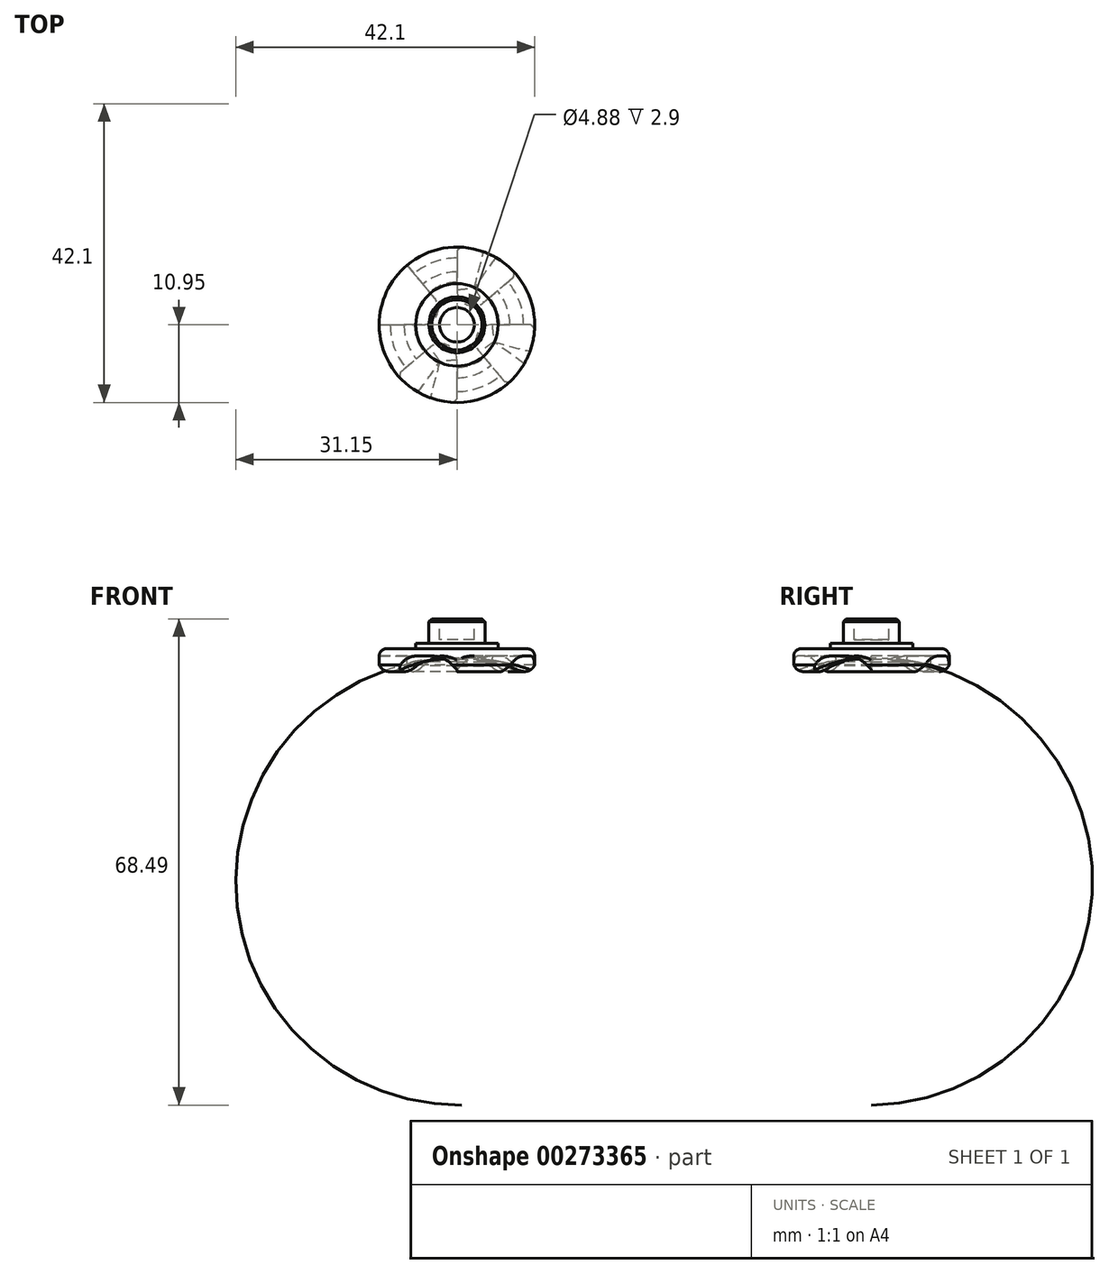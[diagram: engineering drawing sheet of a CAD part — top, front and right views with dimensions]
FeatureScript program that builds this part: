
annotation { "Feature Type Name" : "Feature", "Feature Type Description" : "" }
export const myFeature = defineFeature(function(context is Context, id is Id, definition is map)
    precondition{}
    {
        {
            var Q0;
            Q0=qCreatedBy(makeId("Top.planeOp"),FACE);
            var sketch = newSketch(context, id + "F0", { "sketchPlane" : qUnion([Q0])});
            skCircle(sketch, "E0", {"center": v(0, 0) * mm, "radius": 10.95 * mm});
            skSolve(sketch);
        }
        {
            var Q0;
            Q0=makeQuery(id+"F0.imprint","IMPRINT",FACE,{"disambiguationData":[TD([[makeQuery(id+"F0.imprint","IMPRINT",EDGE,{"derivedFrom":sQuery(id+"F0.wireOp",EDGE,"E0")}),1.0]])]});
            extrude(context, id + "F1", {"entities" : qUnion([Q0]), "depth" : 1 * mm, "offsetDistance" : 25 * mm});
        }
        {
            var Q0;
            Q0=makeQuery(id+"F1.opExtrude","CAP_FACE",FACE,{"disambiguationData":[OSD([sQuery(id+"F0.wireOp",EDGE,"E0")])],"isStart":true});
            var sketch = newSketch(context, id + "F2", { "sketchPlane" : qUnion([Q0])});
            skLineSegment(sketch, "E1", {"start": v(-10.95, 0) * mm, "end": v(-4.95, 0) * mm});
            skLineSegment(sketch, "E2", {"start": v(-7.04, -8.39) * mm, "end": v(-3.18, -3.8) * mm});
            skArc(sketch, "E3", {"start": v(-3.18, -3.8) * mm, "mid": v(-2.86, -1.33) * mm, "end": v(-4.95, 0) * mm});
            skArc(sketch, "E4.1.0", {"start": v(3.8, -3.18) * mm, "mid": v(1.33, -2.86) * mm, "end": v(0, -4.95) * mm});
            skLineSegment(sketch, "E4.1.1", {"start": v(8.39, -7.04) * mm, "end": v(3.8, -3.18) * mm});
            skLineSegment(sketch, "E4.1.2", {"start": v(0, -10.95) * mm, "end": v(0, -4.95) * mm});
            skArc(sketch, "E4.2.0", {"start": v(3.18, 3.8) * mm, "mid": v(2.86, 1.33) * mm, "end": v(4.95, 0) * mm});
            skLineSegment(sketch, "E4.2.1", {"start": v(7.04, 8.39) * mm, "end": v(3.18, 3.8) * mm});
            skLineSegment(sketch, "E4.2.2", {"start": v(10.95, 0) * mm, "end": v(4.95, 0) * mm});
            skArc(sketch, "E4.3.0", {"start": v(-3.8, 3.18) * mm, "mid": v(-1.33, 2.86) * mm, "end": v(0, 4.95) * mm});
            skLineSegment(sketch, "E4.3.1", {"start": v(-8.39, 7.04) * mm, "end": v(-3.8, 3.18) * mm});
            skLineSegment(sketch, "E4.3.2", {"start": v(0, 10.95) * mm, "end": v(0, 4.95) * mm});
            skPoint(sketch, "E4.center", {"position": v(0, 0) * mm});
            skSolve(sketch);
        }
        {
            var Q0;
            {var subQ4=sQuery(id+"F2.wireOp",EDGE,"E1");Q0=makeQuery(id+"F2.imprint","IMPRINT",FACE,{"disambiguationData":[TD([[makeQuery(id+"F2.imprint","IMPRINT",EDGE,{"derivedFrom":subQ4}),1.0]])]});}
            extrude(context, id + "F3", {"entities" : qUnion([Q0]), "operationType" : NewBodyOperationType.ADD, "depth" : 2.8 * mm, "offsetDistance" : 25 * mm});
        }
        {
            var Q0;
            Q0=makeQuery(id+"F1.opExtrude","CAP_FACE",FACE,{"disambiguationData":[OSD([sQuery(id+"F0.wireOp",EDGE,"E0")])],"isStart":false});
            var sketch = newSketch(context, id + "F4", { "sketchPlane" : qUnion([Q0])});
            skCircle(sketch, "E5", {"center": v(0, 0) * mm, "radius": 3.94 * mm});
            skSolve(sketch);
        }
        {
            var Q0;
            Q0=makeQuery(id+"F4.imprint","IMPRINT",FACE,{"disambiguationData":[TD([[makeQuery(id+"F4.imprint","IMPRINT",EDGE,{"derivedFrom":sQuery(id+"F4.wireOp",EDGE,"E5")}),1.0]])]});
            extrude(context, id + "F5", {"entities" : qUnion([Q0]), "operationType" : NewBodyOperationType.ADD, "depth" : 4.2 * mm, "offsetDistance" : 25 * mm});
        }
        {
            var Q0;
            Q0=makeQuery(id+"F1.opExtrude","CAP_EDGE",EDGE,{"disambiguationData":[OSD([sQuery(id+"F0.wireOp",EDGE,"E0")])],"isStart":false});
            fillet(context, id + "F6", {"entities" : qUnion([Q0]), "radius" : 1 * mm, "tangentPropagation" : true, "allowEdgeOverflow" : false});
        }
        {
            var Q0;
            Q0=makeQuery(id+"F1.opExtrude","CAP_FACE",FACE,{"disambiguationData":[OSD([sQuery(id+"F0.wireOp",EDGE,"E0")])],"isStart":false});
            var sketch = newSketch(context, id + "F7", { "sketchPlane" : qUnion([Q0])});
            skCircle(sketch, "E6", {"center": v(0, 0) * mm, "radius": 5.8 * mm});
            skSolve(sketch);
        }
        {
            var Q0;
            Q0=makeQuery(id+"F7.imprint","IMPRINT",FACE,{"disambiguationData":[TD([[makeQuery(id+"F7.imprint","IMPRINT",EDGE,{"derivedFrom":sQuery(id+"F7.wireOp",EDGE,"E6")}),1.0]])]});
            extrude(context, id + "F8", {"entities" : qUnion([Q0]), "operationType" : NewBodyOperationType.ADD, "depth" : .8 * mm, "offsetDistance" : 25 * mm});
        }
        {
            var Q0;
            Q0=makeQuery(id+"F5.opExtrude","CAP_FACE",FACE,{"disambiguationData":[OSD([sQuery(id+"F4.wireOp",EDGE,"E5")])],"isStart":false});
            var sketch = newSketch(context, id + "F9", { "sketchPlane" : qUnion([Q0])});
            skCircle(sketch, "E7", {"center": v(0, 0) * mm, "radius": 2.44 * mm});
            skSolve(sketch);
        }
        {
            var Q0;
            Q0=makeQuery(id+"F9.imprint","IMPRINT",FACE,{"disambiguationData":[TD([[makeQuery(id+"F9.imprint","IMPRINT",EDGE,{"derivedFrom":sQuery(id+"F9.wireOp",EDGE,"E7")}),1.0]])]});
            extrude(context, id + "F10", {"entities" : qUnion([Q0]), "operationType" : NewBodyOperationType.REMOVE, "oppositeDirection" : true, "depth" : 2.9 * mm, "offsetDistance" : 25 * mm});
        }
        {
            var Q0;
            Q0=qCreatedBy(makeId("Right.planeOp"),FACE);
            var sketch = newSketch(context, id + "F11", { "sketchPlane" : qUnion([Q0])});
            skLineSegment(sketch, "E8", {"start": v(-11.4, 0) * mm, "end": v(-10, 0) * mm, "construction": true});
            skLineSegment(sketch, "E9", {"start": v(0, -3.5) * mm, "end": v(0, -0.3) * mm});
            skLineSegment(sketch, "E10", {"start": v(0, -3.5) * mm, "end": v(-10, -3.5) * mm});
            skLineSegment(sketch, "E11", {"start": v(-10, -3.5) * mm, "end": v(-11.62, -3.5) * mm});
            skLineSegment(sketch, "E12", {"start": v(-11.62, -3.5) * mm, "end": v(-11.06, -0.4) * mm});
            skArc(sketch, "E13", {"start": v(-11.06, -0.4) * mm, "mid": v(-10.68, -1.71) * mm, "end": v(-9.4, -2.2) * mm});
            skArc(sketch, "E14", {"start": v(-9.4, -2.2) * mm, "mid": v(-8.38, -1.93) * mm, "end": v(-7.46, -1.41) * mm});
            skArc(sketch, "E15", {"start": v(-6, -0.8) * mm, "mid": v(-6.75, -1.06) * mm, "end": v(-7.46, -1.41) * mm});
            skArc(sketch, "E16", {"start": v(0, -0.3) * mm, "mid": v(-3, -0.41) * mm, "end": v(-6, -0.8) * mm});
            skSolve(sketch);
        }
        {
            var Q0;
            Q0=makeQuery(id+"F11.imprint","IMPRINT",FACE,{"disambiguationData":[TD([[makeQuery(id+"F11.imprint","IMPRINT",EDGE,{"derivedFrom":sQuery(id+"F11.wireOp",EDGE,"E9")}),1.0]])]});
            var Q1;
            Q1=sQuery(id+"F11.wireOp",EDGE,"E9");
            revolve(context, id + "F12", {"operationType" : NewBodyOperationType.REMOVE, "entities" : qUnion([Q0]), "axis" : qUnion([Q1]), "revolveType" : RevolveType.FULL, "oppositeDirection" : true});
        }
        {
            var Q0;
            Q0=makeQuery(id+"F5.opExtrude","CAP_EDGE",EDGE,{"disambiguationData":[OSD([sQuery(id+"F4.wireOp",EDGE,"E5")])],"isStart":false});
            chamfer(context, id + "F13", {"entities" : qUnion([Q0]), "width" : .4 * mm, "tangentPropagation" : true});
        }
        {
            var Q0;
            Q0=makeQuery(id+"F3.opExtrude","CAP_EDGE",EDGE,{"disambiguationData":[OSD([sQuery(id+"F2.wireOp",EDGE,"E4.3.0")])],"isStart":true});
            var Q1;
            Q1=makeQuery(id+"F3.opExtrude","CAP_EDGE",EDGE,{"disambiguationData":[OSD([sQuery(id+"F2.wireOp",EDGE,"E3")])],"isStart":true});
            var Q2;
            Q2=makeQuery(id+"F3.opExtrude","CAP_EDGE",EDGE,{"disambiguationData":[OSD([sQuery(id+"F2.wireOp",EDGE,"E4.1.0")])],"isStart":true});
            var Q3;
            Q3=makeQuery(id+"F3.opExtrude","CAP_EDGE",EDGE,{"disambiguationData":[OSD([sQuery(id+"F2.wireOp",EDGE,"E4.2.0")])],"isStart":true});
            fillet(context, id + "F14", {"entities" : qUnion([Q0, Q1, Q2, Q3]), "radius" : 4.4 * mm, "tangentPropagation" : true, "rho" : 0.5, "crossSection" : FilletCrossSection.CONIC, "allowEdgeOverflow" : false});
        }
    });
